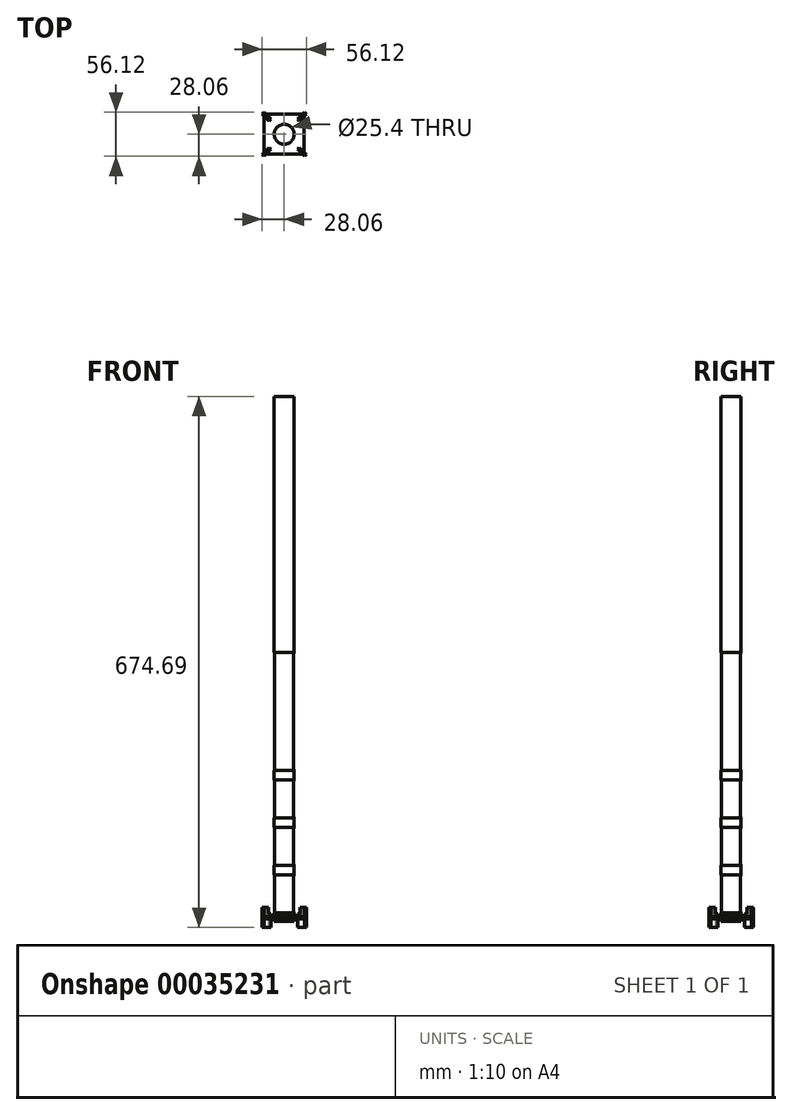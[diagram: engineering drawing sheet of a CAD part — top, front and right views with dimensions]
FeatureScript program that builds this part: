
annotation { "Feature Type Name" : "Feature", "Feature Type Description" : "" }
export const myFeature = defineFeature(function(context is Context, id is Id, definition is map)
    precondition{}
    {
        {
            var Q0;
            Q0=qCreatedBy(makeId("Top.planeOp"),FACE);
            var sketch = newSketch(context, id + "F0", { "sketchPlane" : qUnion([Q0])});
            skLineSegment(sketch, "E0.bottom", {"start": v(-25.4, -25.4) * mm, "end": v(25.4, -25.4) * mm});
            skLineSegment(sketch, "E0.top", {"start": v(-25.4, 25.4) * mm, "end": v(25.4, 25.4) * mm});
            skLineSegment(sketch, "E0.left", {"start": v(-25.4, -25.4) * mm, "end": v(-25.4, 25.4) * mm});
            skLineSegment(sketch, "E0.right", {"start": v(25.4, -25.4) * mm, "end": v(25.4, 25.4) * mm});
            skCircle(sketch, "E1", {"center": v(0, 0) * mm, "radius": 12.7 * mm});
            skSolve(sketch);
        }
        {
            var Q0;
            Q0=makeQuery(id+"F0.imprint","IMPRINT",FACE,{"disambiguationData":[TD([[makeQuery(id+"F0.imprint","IMPRINT",EDGE,{"derivedFrom":sQuery(id+"F0.wireOp",EDGE,"E0.bottom")}),1.0]])]});
            extrude(context, id + "F1", {"entities" : qUnion([Q0]), "oppositeDirection" : true, "depth" : 3.17 * mm});
        }
        {
            var Q0;
            Q0=qCreatedBy(makeId("Front.planeOp"),FACE);
            var sketch = newSketch(context, id + "F2", { "sketchPlane" : qUnion([Q0])});
            skLineSegment(sketch, "E2.bottom", {"start": v(25.4, -14.29) * mm, "end": v(38.1, -14.29) * mm});
            skLineSegment(sketch, "E2.top", {"start": v(25.4, 11.11) * mm, "end": v(38.1, 11.11) * mm});
            skLineSegment(sketch, "E2.left", {"start": v(25.4, -14.29) * mm, "end": v(25.4, 11.11) * mm});
            skLineSegment(sketch, "E2.right", {"start": v(38.1, -14.29) * mm, "end": v(38.1, 11.11) * mm});
            skSolve(sketch);
        }
        {
            var Q0;
            Q0=makeQuery(id+"F2.imprint","IMPRINT",FACE,{"disambiguationData":[TD([[makeQuery(id+"F2.imprint","IMPRINT",EDGE,{"derivedFrom":sQuery(id+"F2.wireOp",EDGE,"E2.bottom")}),1.0]])]});
            extrude(context, id + "F3", {"entities" : qUnion([Q0]), "endBound" : BoundingType.SYMMETRIC, "depth" : 3.17 * mm});
        }
        {
            var Q0;
            Q0=makeQuery(id+"F3.opExtrude","SWEPT_BODY",BODY,{"disambiguationData":[OSD([sQuery(id+"F2.wireOp",EDGE,"E2.bottom"),sQuery(id+"F2.wireOp",EDGE,"E2.top"),sQuery(id+"F2.wireOp",EDGE,"E2.left"),sQuery(id+"F2.wireOp",EDGE,"E2.right")])]});
            var Q1;
            Q1=makeQuery(id+"F1.opExtrude","CAP_EDGE",EDGE,{"disambiguationData":[OSD([sQuery(id+"F0.wireOp",EDGE,"E1")])],"isStart":true});
            circularPattern(context, id + "F4", {"entities" : qUnion([Q0]), "axis" : qUnion([Q1]), "angle" : 90 * degree, "instanceCount" : 4, "oppositeDirection" : true});
        }
        {
            var Q0;
            Q0=makeQuery(id+"F3.opExtrude","SWEPT_BODY",BODY,{"disambiguationData":[OSD([sQuery(id+"F2.wireOp",EDGE,"E2.bottom"),sQuery(id+"F2.wireOp",EDGE,"E2.top"),sQuery(id+"F2.wireOp",EDGE,"E2.left"),sQuery(id+"F2.wireOp",EDGE,"E2.right")])]});
            var Q1;
            Q1=makeQuery(id+"F4.opPattern","COPY",BODY,{"derivedFrom":makeQuery(id+"F3.opExtrude","SWEPT_BODY",BODY,{"disambiguationData":[OSD([sQuery(id+"F2.wireOp",EDGE,"E2.bottom"),sQuery(id+"F2.wireOp",EDGE,"E2.top"),sQuery(id+"F2.wireOp",EDGE,"E2.left"),sQuery(id+"F2.wireOp",EDGE,"E2.right")])]}),"instanceName":"1"});
            var Q2;
            Q2=makeQuery(id+"F4.opPattern","COPY",BODY,{"derivedFrom":makeQuery(id+"F3.opExtrude","SWEPT_BODY",BODY,{"disambiguationData":[OSD([sQuery(id+"F2.wireOp",EDGE,"E2.bottom"),sQuery(id+"F2.wireOp",EDGE,"E2.top"),sQuery(id+"F2.wireOp",EDGE,"E2.left"),sQuery(id+"F2.wireOp",EDGE,"E2.right")])]}),"instanceName":"2"});
            var Q3;
            Q3=makeQuery(id+"F4.opPattern","COPY",BODY,{"derivedFrom":makeQuery(id+"F3.opExtrude","SWEPT_BODY",BODY,{"disambiguationData":[OSD([sQuery(id+"F2.wireOp",EDGE,"E2.bottom"),sQuery(id+"F2.wireOp",EDGE,"E2.top"),sQuery(id+"F2.wireOp",EDGE,"E2.left"),sQuery(id+"F2.wireOp",EDGE,"E2.right")])]}),"instanceName":"3"});
            var Q4;
            Q4=makeQuery(id+"F1.opExtrude","CAP_EDGE",EDGE,{"disambiguationData":[OSD([sQuery(id+"F0.wireOp",EDGE,"E1")])],"isStart":true});
            transform(context, id + "F5", {"entities" : qUnion([Q0, Q1, Q2, Q3]), "transformType" : TransformType.ROTATION, "transformAxis" : qUnion([Q4]), "angle" : 45 * degree, "makeCopy" : false});
        }
        {
            var Q0;
            Q0=makeQuery(id+"F4.opPattern","COPY",BODY,{"derivedFrom":makeQuery(id+"F3.opExtrude","SWEPT_BODY",BODY,{"disambiguationData":[OSD([sQuery(id+"F2.wireOp",EDGE,"E2.bottom"),sQuery(id+"F2.wireOp",EDGE,"E2.top"),sQuery(id+"F2.wireOp",EDGE,"E2.left"),sQuery(id+"F2.wireOp",EDGE,"E2.right")])]}),"instanceName":"2"});
            var Q1;
            Q1=makeQuery(id+"F4.opPattern","COPY",BODY,{"derivedFrom":makeQuery(id+"F3.opExtrude","SWEPT_BODY",BODY,{"disambiguationData":[OSD([sQuery(id+"F2.wireOp",EDGE,"E2.bottom"),sQuery(id+"F2.wireOp",EDGE,"E2.top"),sQuery(id+"F2.wireOp",EDGE,"E2.left"),sQuery(id+"F2.wireOp",EDGE,"E2.right")])]}),"instanceName":"1"});
            var Q2;
            Q2=makeQuery(id+"F3.opExtrude","SWEPT_BODY",BODY,{"disambiguationData":[OSD([sQuery(id+"F2.wireOp",EDGE,"E2.bottom"),sQuery(id+"F2.wireOp",EDGE,"E2.top"),sQuery(id+"F2.wireOp",EDGE,"E2.left"),sQuery(id+"F2.wireOp",EDGE,"E2.right")])]});
            var Q3;
            Q3=makeQuery(id+"F4.opPattern","COPY",BODY,{"derivedFrom":makeQuery(id+"F3.opExtrude","SWEPT_BODY",BODY,{"disambiguationData":[OSD([sQuery(id+"F2.wireOp",EDGE,"E2.bottom"),sQuery(id+"F2.wireOp",EDGE,"E2.top"),sQuery(id+"F2.wireOp",EDGE,"E2.left"),sQuery(id+"F2.wireOp",EDGE,"E2.right")])]}),"instanceName":"3"});
            var Q4;
            Q4=makeQuery(id+"F1.opExtrude","SWEPT_BODY",BODY,{"disambiguationData":[OSD([sQuery(id+"F0.wireOp",EDGE,"E0.bottom"),sQuery(id+"F0.wireOp",EDGE,"E0.top"),sQuery(id+"F0.wireOp",EDGE,"E0.left"),sQuery(id+"F0.wireOp",EDGE,"E0.right"),sQuery(id+"F0.wireOp",EDGE,"E1")])]});
            booleanBodies(context, id + "F6", {"operationType" : BooleanOperationType.SUBTRACTION, "tools" : qUnion([Q0, Q1, Q2, Q3]), "targets" : qUnion([Q4]), "keepTools" : true});
        }
        {
            var Q0;
            Q0=qCreatedBy(makeId("Top.planeOp"),FACE);
            var sketch = newSketch(context, id + "F7", { "sketchPlane" : qUnion([Q0])});
            skCircle(sketch, "E3", {"center": v(0, 0) * mm, "radius": 12.69 * mm});
            skSolve(sketch);
        }
        {
            var Q0;
            Q0 = qSketchRegion(id + "F7", true);
            extrude(context, id + "F8", {"entities" : qUnion([Q0]), "depth" : 660.4 * mm});
        }
        {
            var Q0;
            Q0 = qSketchRegion(id + "F7", true);
            extrude(context, id + "F9", {"entities" : qUnion([Q0]), "operationType" : NewBodyOperationType.ADD, "oppositeDirection" : true, "depth" : 6.35 * mm});
        }
        {
            var Q0;
            Q0=qCreatedBy(makeId("Front.planeOp"),FACE);
            var sketch = newSketch(context, id + "F10", { "sketchPlane" : qUnion([Q0])});
            skLineSegment(sketch, "E4.rect.bottom", {"start": v(30.08, 3.18) * mm, "end": v(15.24, 3.18) * mm});
            skLineSegment(sketch, "E4.rect.top", {"start": v(30.08, 53.98) * mm, "end": v(15.24, 53.98) * mm});
            skLineSegment(sketch, "E4.rect.left", {"start": v(30.08, 3.18) * mm, "end": v(30.08, 53.98) * mm});
            skLineSegment(sketch, "E4.rect.right", {"start": v(12.06, 6.35) * mm, "end": v(12.06, 50.8) * mm});
            skPoint(sketch, "E4.rect.middle", {"position": v(21.07, 28.58) * mm});
            skPoint(sketch, "E5.visualSharp", {"position": v(12.06, 53.98) * mm});
            skArc(sketch, "E5.filletArc", {"start": v(15.24, 53.98) * mm, "mid": v(13, 53.05) * mm, "end": v(12.06, 50.8) * mm});
            skPoint(sketch, "E6.visualSharp", {"position": v(12.06, 3.18) * mm});
            skArc(sketch, "E6.filletArc", {"start": v(12.06, 6.35) * mm, "mid": v(13, 4.1) * mm, "end": v(15.24, 3.18) * mm});
            skSolve(sketch);
        }
        {
            var Q0;
            Q0=qCreatedBy(makeId("Front.planeOp"),FACE);
            var sketch = newSketch(context, id + "F11", { "sketchPlane" : qUnion([Q0])});
            skLineSegment(sketch, "E7.rect.bottom", {"start": v(30.08, 63.5) * mm, "end": v(15.24, 63.5) * mm});
            skLineSegment(sketch, "E7.rect.top", {"start": v(30.08, 114.3) * mm, "end": v(15.24, 114.3) * mm});
            skLineSegment(sketch, "E7.rect.left", {"start": v(30.08, 63.5) * mm, "end": v(30.08, 114.3) * mm});
            skLineSegment(sketch, "E7.rect.right", {"start": v(12.06, 66.68) * mm, "end": v(12.06, 111.13) * mm});
            skPoint(sketch, "E7.rect.middle", {"position": v(21.07, 88.9) * mm});
            skPoint(sketch, "E8.visualSharp", {"position": v(12.06, 114.3) * mm});
            skArc(sketch, "E8.filletArc", {"start": v(15.24, 114.3) * mm, "mid": v(13, 113.37) * mm, "end": v(12.06, 111.13) * mm});
            skPoint(sketch, "E9.visualSharp", {"position": v(12.06, 63.5) * mm});
            skArc(sketch, "E9.filletArc", {"start": v(12.06, 66.68) * mm, "mid": v(13, 64.43) * mm, "end": v(15.24, 63.5) * mm});
            skSolve(sketch);
        }
        {
            var Q0;
            Q0=qCreatedBy(makeId("Front.planeOp"),FACE);
            var sketch = newSketch(context, id + "F12", { "sketchPlane" : qUnion([Q0])});
            skLineSegment(sketch, "E10.rect.bottom", {"start": v(30.08, 123.83) * mm, "end": v(15.24, 123.83) * mm});
            skLineSegment(sketch, "E10.rect.top", {"start": v(30.08, 174.63) * mm, "end": v(15.24, 174.63) * mm});
            skLineSegment(sketch, "E10.rect.left", {"start": v(30.08, 123.83) * mm, "end": v(30.08, 174.63) * mm});
            skLineSegment(sketch, "E10.rect.right", {"start": v(12.06, 127) * mm, "end": v(12.06, 171.45) * mm});
            skPoint(sketch, "E10.rect.middle", {"position": v(21.07, 149.23) * mm});
            skPoint(sketch, "E11.visualSharp", {"position": v(12.06, 174.63) * mm});
            skArc(sketch, "E11.filletArc", {"start": v(15.24, 174.63) * mm, "mid": v(13, 173.7) * mm, "end": v(12.06, 171.45) * mm});
            skPoint(sketch, "E12.visualSharp", {"position": v(12.06, 123.83) * mm});
            skArc(sketch, "E12.filletArc", {"start": v(12.06, 127) * mm, "mid": v(13, 124.75) * mm, "end": v(15.24, 123.83) * mm});
            skSolve(sketch);
        }
        {
            var Q0;
            Q0 = qSketchRegion(id + "F10", true);
            var Q1;
            Q1=makeQuery(id+"F8.opExtrude","CAP_EDGE",EDGE,{"disambiguationData":[OSD([sQuery(id+"F7.wireOp",EDGE,"E3")])],"isStart":false});
            revolve(context, id + "F13", {"operationType" : NewBodyOperationType.REMOVE, "entities" : qUnion([Q0]), "axis" : qUnion([Q1]), "revolveType" : RevolveType.FULL, "oppositeDirection" : true});
        }
        {
            var Q0;
            Q0=makeQuery(id+"F11.imprint","IMPRINT",FACE,{"disambiguationData":[TD([[makeQuery(id+"F11.imprint","IMPRINT",EDGE,{"derivedFrom":sQuery(id+"F11.wireOp",EDGE,"E7.rect.bottom")}),-1.0]])]});
            var Q1;
            Q1=makeQuery(id+"F8.opExtrude","CAP_EDGE",EDGE,{"disambiguationData":[OSD([sQuery(id+"F7.wireOp",EDGE,"E3")])],"isStart":false});
            revolve(context, id + "F14", {"operationType" : NewBodyOperationType.REMOVE, "entities" : qUnion([Q0]), "axis" : qUnion([Q1]), "revolveType" : RevolveType.FULL, "oppositeDirection" : true});
        }
        {
            var Q0;
            Q0=makeQuery(id+"F12.imprint","IMPRINT",FACE,{"disambiguationData":[TD([[makeQuery(id+"F12.imprint","IMPRINT",EDGE,{"derivedFrom":sQuery(id+"F12.wireOp",EDGE,"E10.rect.bottom")}),-1.0]])]});
            var Q1;
            Q1=makeQuery(id+"F8.opExtrude","CAP_EDGE",EDGE,{"disambiguationData":[OSD([sQuery(id+"F7.wireOp",EDGE,"E3")])],"isStart":false});
            revolve(context, id + "F15", {"operationType" : NewBodyOperationType.REMOVE, "entities" : qUnion([Q0]), "axis" : qUnion([Q1]), "revolveType" : RevolveType.FULL, "oppositeDirection" : true});
        }
        {
            var Q0;
            Q0 = qSketchRegion(id + "F11", true);
            var sketch = newSketch(context, id + "F16", { "sketchPlane" : qUnion([Q0])});
            skLineSegment(sketch, "E13.rect.bottom", {"start": v(30.08, 184.15) * mm, "end": v(15.24, 184.15) * mm});
            skLineSegment(sketch, "E13.rect.top", {"start": v(30.08, 336.55) * mm, "end": v(15.24, 336.55) * mm});
            skLineSegment(sketch, "E13.rect.left", {"start": v(30.08, 184.15) * mm, "end": v(30.08, 336.55) * mm});
            skLineSegment(sketch, "E13.rect.right", {"start": v(12.06, 187.33) * mm, "end": v(12.06, 333.38) * mm});
            skPoint(sketch, "E13.rect.middle", {"position": v(21.07, 260.35) * mm});
            skPoint(sketch, "E14.visualSharp", {"position": v(12.06, 336.55) * mm});
            skArc(sketch, "E14.filletArc", {"start": v(15.24, 336.55) * mm, "mid": v(13, 335.62) * mm, "end": v(12.06, 333.38) * mm});
            skPoint(sketch, "E15.visualSharp", {"position": v(12.06, 184.15) * mm});
            skArc(sketch, "E15.filletArc", {"start": v(12.06, 187.33) * mm, "mid": v(13, 185.08) * mm, "end": v(15.24, 184.15) * mm});
            skSolve(sketch);
        }
        {
            var Q0;
            Q0=makeQuery(id+"F16.imprint","IMPRINT",FACE,{"disambiguationData":[TD([[makeQuery(id+"F16.imprint","IMPRINT",EDGE,{"derivedFrom":sQuery(id+"F16.wireOp",EDGE,"E13.rect.bottom")}),-1.0]])]});
            var Q1;
            {var subQ0=sQuery(id+"F7.wireOp",EDGE,"E3");var subQ1=makeQuery(id+"F8.opExtrude","CAP_FACE",FACE,{"disambiguationData":[OSD([subQ0])],"isStart":false});Q1=makeQuery(id+"F15.boolean.opBoolean","SPLIT",FACE,{"disambiguationData":[TD([subQ1])],"derivedFrom":makeQuery(id+"F14.boolean.opBoolean","SPLIT",FACE,{"disambiguationData":[TD([subQ1])],"derivedFrom":makeQuery(id+"F13.boolean.opBoolean","SPLIT",FACE,{"disambiguationData":[TD([subQ1])],"derivedFrom":makeQuery(id+"F9.boolean.opBoolean","MERGE",FACE,{"derivedFrom":[makeQuery(id+"F8.opExtrude","SWEPT_FACE",FACE,{"disambiguationData":[OSD([subQ0])]}),makeQuery(id+"F9.opExtrude","SWEPT_FACE",FACE,{"disambiguationData":[OSD([subQ0])]})]})})})});}
            revolve(context, id + "F17", {"operationType" : NewBodyOperationType.REMOVE, "entities" : qUnion([Q0]), "axis" : qUnion([Q1]), "revolveType" : RevolveType.FULL, "oppositeDirection" : true});
        }
    });
